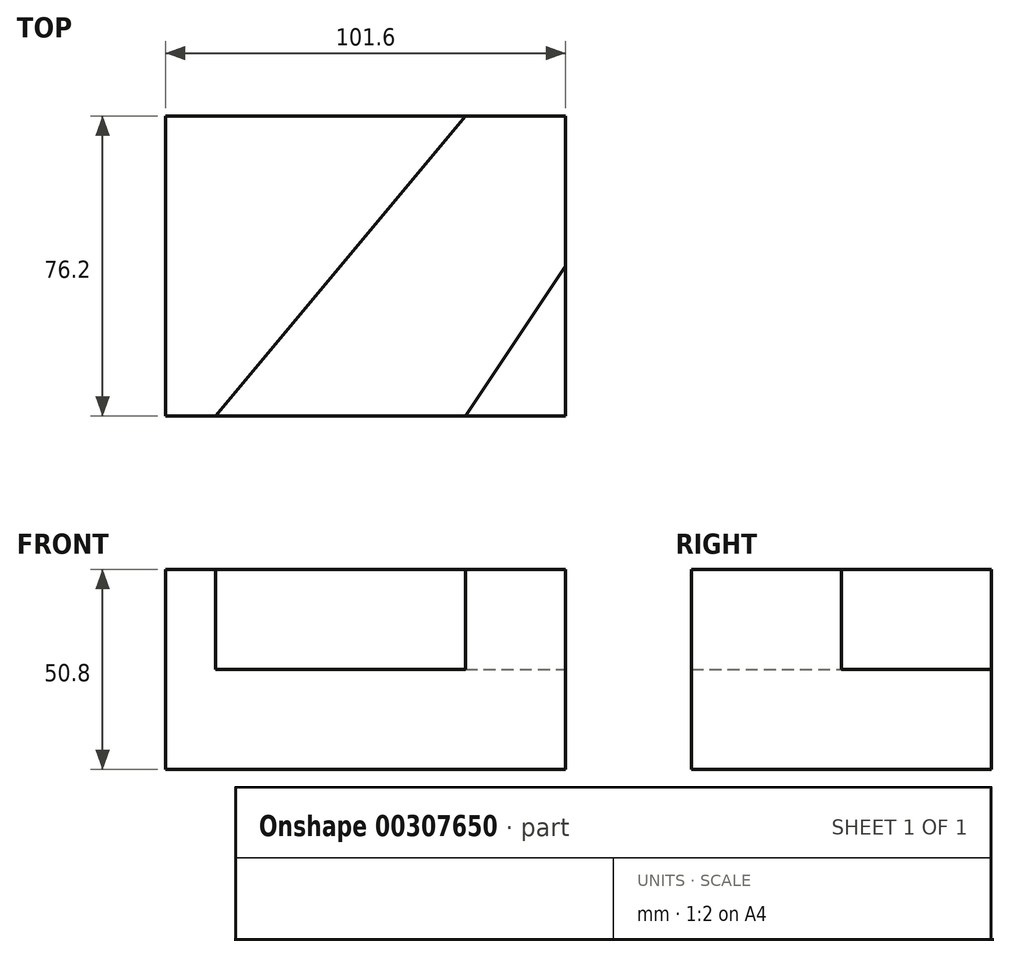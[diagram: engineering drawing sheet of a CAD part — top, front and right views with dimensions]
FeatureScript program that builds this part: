
annotation { "Feature Type Name" : "Feature", "Feature Type Description" : "" }
export const myFeature = defineFeature(function(context is Context, id is Id, definition is map)
    precondition{}
    {
        {
            var Q0;
            Q0=qCreatedBy(makeId("Front.planeOp"),FACE);
            var sketch = newSketch(context, id + "F0", { "sketchPlane" : qUnion([Q0])});
            skLineSegment(sketch, "E0", {"start": v(-55.7, -50.76) * mm, "end": v(45.9, -50.76) * mm});
            skLineSegment(sketch, "E1", {"start": v(45.9, -50.76) * mm, "end": v(45.9, -25.36) * mm});
            skLineSegment(sketch, "E2", {"start": v(45.9, -25.36) * mm, "end": v(-55.7, -25.36) * mm});
            skLineSegment(sketch, "E3", {"start": v(-55.7, -25.36) * mm, "end": v(-55.7, -50.76) * mm});
            skSolve(sketch);
        }
        {
            var Q0;
            Q0=makeQuery(id+"F0.imprint","IMPRINT",FACE,{"disambiguationData":[TD([[makeQuery(id+"F0.imprint","IMPRINT",EDGE,{"derivedFrom":sQuery(id+"F0.wireOp",EDGE,"E0")}),1.0]])]});
            extrude(context, id + "F1", {"entities" : qUnion([Q0]), "depth" : 76.2 * mm});
        }
        {
            var Q0;
            Q0=makeQuery(id+"F1.opExtrude","SWEPT_FACE",FACE,{"disambiguationData":[OSD([sQuery(id+"F0.wireOp",EDGE,"E2")])]});
            var sketch = newSketch(context, id + "F2", { "sketchPlane" : qUnion([Q0])});
            skLineSegment(sketch, "E4", {"start": v(45.9, -76.2) * mm, "end": v(45.9, -38.1) * mm});
            skLineSegment(sketch, "E5", {"start": v(45.9, -76.2) * mm, "end": v(20.5, -76.2) * mm});
            skLineSegment(sketch, "E6", {"start": v(20.5, -76.2) * mm, "end": v(45.9, -38.1) * mm});
            skSolve(sketch);
        }
        {
            var Q0;
            Q0=makeQuery(id+"F2.imprint","IMPRINT",FACE,{"disambiguationData":[TD([[makeQuery(id+"F2.imprint","IMPRINT",EDGE,{"derivedFrom":sQuery(id+"F2.wireOp",EDGE,"E4")}),1.0]])]});
            extrude(context, id + "F3", {"entities" : qUnion([Q0]), "operationType" : NewBodyOperationType.ADD, "depth" : 25.4 * mm});
        }
        {
            var Q0;
            Q0=makeQuery(id+"F1.opExtrude","SWEPT_FACE",FACE,{"disambiguationData":[OSD([sQuery(id+"F0.wireOp",EDGE,"E2")])]});
            var sketch = newSketch(context, id + "F4", { "sketchPlane" : qUnion([Q0])});
            skLineSegment(sketch, "E7", {"start": v(-55.7, -76.2) * mm, "end": v(-43, -76.2) * mm});
            skLineSegment(sketch, "E8", {"start": v(-43, -76.2) * mm, "end": v(20.5, 0) * mm});
            skLineSegment(sketch, "E9", {"start": v(20.5, 0) * mm, "end": v(-55.7, 0) * mm});
            skLineSegment(sketch, "E10", {"start": v(-55.7, 0) * mm, "end": v(-55.7, -76.2) * mm});
            skSolve(sketch);
        }
        {
            var Q0;
            Q0=makeQuery(id+"F4.imprint","IMPRINT",FACE,{"disambiguationData":[TD([[makeQuery(id+"F4.imprint","IMPRINT",EDGE,{"derivedFrom":sQuery(id+"F4.wireOp",EDGE,"E7")}),-1.0]])]});
            extrude(context, id + "F5", {"entities" : qUnion([Q0]), "operationType" : NewBodyOperationType.ADD, "depth" : 25.4 * mm});
        }
    });
